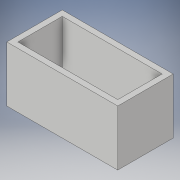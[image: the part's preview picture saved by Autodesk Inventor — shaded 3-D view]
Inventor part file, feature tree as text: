
AUTODESK INVENTOR PART (.ipt)
format: ipt  version: 2019 (Build 230136000, 136)  size: 91,648 bytes
history: native  units: in
note: dims shown in document units (in); Inventor stores cm internally (conversion verified against a paired STEP export)
features: extrude x1, shell x1, sketch x1
ambient origin geometry x8: Origin, YZ Plane, XZ Plane, XY Plane, X Axis, Y Axis, Z Axis, Center Point
bodies: Solid1 (feature_tree)
feature tree (3):
  extrude  "Extrusion1"  Depth=3.0in
  shell  "Shell1"  Thickness=3.0in
  sketch  "Sketch1"  dims[d0=6.0in d1=3.0in d2=3.0in d3=0.0in d4=0.3in]
